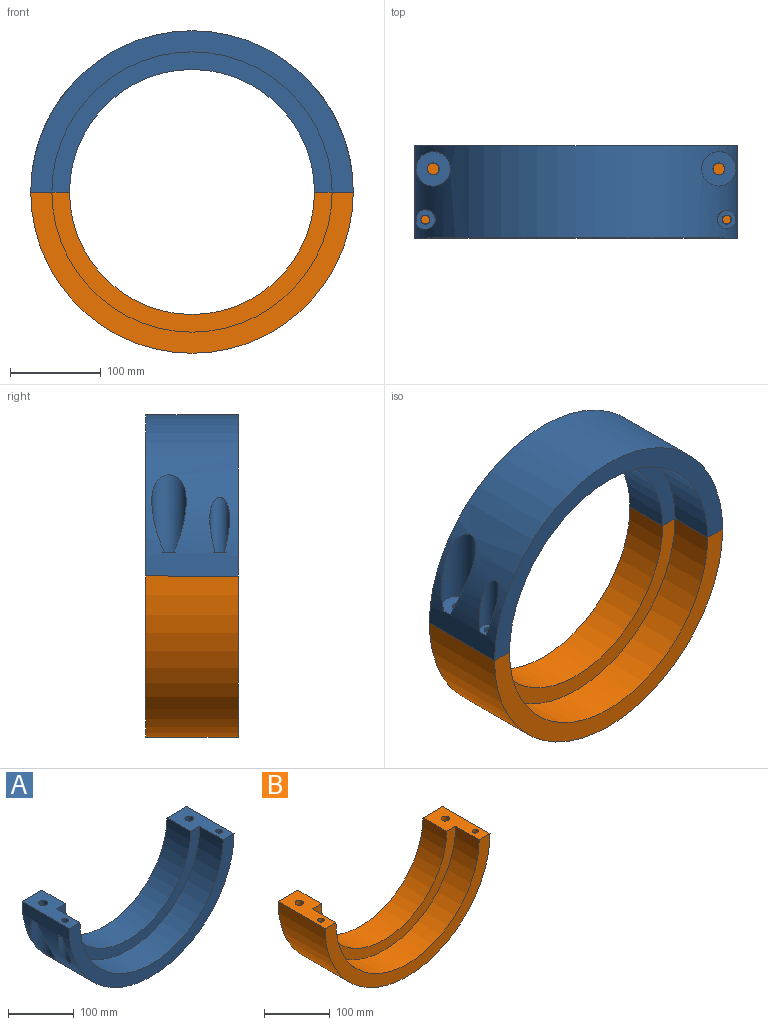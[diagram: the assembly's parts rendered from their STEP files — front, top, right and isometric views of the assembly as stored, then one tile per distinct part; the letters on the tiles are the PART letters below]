
ASSEMBLY  parts=2 mates=1
PART A: 20 faces, bbox 355.6x101.6x177.8 mm
  f0: plane 101.6x42.77mm, normal (0,0,1), area 3138.7mm2, adj f2,f3,f4,f5,f6,f7,f8,f14
  f1: plane 101.6x42.77mm, normal (0,0,1), area 3138.7mm2, adj f2,f3,f4,f5,f6,f7,f9,f15
  f2: cylinder r=177.8mm len=355.6mm, axis (0,1,0), area 49107.8mm2, adj f0,f1,f3,f4,f10,f11,f12,f13
  f3: plane 355.6x177.8mm, normal (0,-1,0), area 12164.2mm2, adj f0,f1,f2,f5
  f4: plane 355.6x177.8mm, normal (0,1,0), area 21018.4mm2, adj f0,f1,f2,f7
  f5: cylinder r=154.5mm len=308.99mm, axis (0,-1,0), area 24656.4mm2, adj f0,f1,f3,f6
  f6: plane 308.99x154.5mm, normal (0,-1,0), area 8854.2mm2, adj f0,f1,f5,f7
  f7: cylinder r=135.03mm len=270.05mm, axis (0,-1,0), area 21549.3mm2, adj f0,f1,f4,f6
  f8: cylinder r=6.6mm len=25.4mm, axis (0,0,1), area 1054mm2, adj f0,f11
  f9: cylinder r=6.6mm len=25.4mm, axis (0,0,1), area 1054mm2, adj f1,f13
  f10: cylinder r=19.05mm len=86.18mm, axis (0,0,1), area 6036.2mm2, adj f2,f11
  f11: plane 38.1x37.55mm, normal (0,0,-1), area 999.7mm2, adj f2,f8,f10
  f12: cylinder r=19.05mm len=86.18mm, axis (0,0,1), area 6036.2mm2, adj f2,f13
  f13: plane 38.1x37.55mm, normal (0,0,-1), area 999.7mm2, adj f2,f9,f12
  f14: cylinder r=5.08mm len=25.4mm, axis (0,0,1), area 810.7mm2, adj f0,f17
  f15: cylinder r=5.08mm len=25.4mm, axis (0,0,1), area 810.7mm2, adj f1,f19
  f16: cylinder r=10.97mm len=61.4mm, axis (0,0,1), area 2318.4mm2, adj f2,f17
  f17: plane 21.94x20.8mm, normal (0,0,-1), area 289.4mm2, adj f2,f14,f16
  f18: cylinder r=10.16mm len=59.93mm, axis (0,0,1), area 2165.5mm2, adj f2,f19
  f19: plane 20.32x19.99mm, normal (0,0,-1), area 242.1mm2, adj f2,f15,f18
PART B: 16 faces, bbox 355.6x101.6x177.8 mm
  f0: plane 101.6x42.77mm, normal (0,0,1), area 3158.8mm2, adj f2,f3,f4,f5,f6,f7,f10,f12
  f1: plane 101.6x42.77mm, normal (0,0,1), area 3158.8mm2, adj f2,f3,f4,f5,f6,f7,f8,f14
  f2: cylinder r=177.8mm len=355.6mm, axis (0,1,0), area 56751.2mm2, adj f0,f1,f3,f4
  f3: plane 355.6x177.8mm, normal (0,-1,0), area 12164.2mm2, adj f0,f1,f2,f5
  f4: plane 355.6x177.8mm, normal (0,1,0), area 21018.4mm2, adj f0,f1,f2,f7
  f5: cylinder r=154.5mm len=308.99mm, axis (0,-1,0), area 24656.4mm2, adj f0,f1,f3,f6
  f6: plane 308.99x154.5mm, normal (0,-1,0), area 8854.2mm2, adj f0,f1,f5,f7
  f7: cylinder r=135.03mm len=270.05mm, axis (0,-1,0), area 21549.3mm2, adj f0,f1,f4,f6
  f8: cylinder r=6.35mm len=25.4mm, axis (0,0,1), area 1013.4mm2, adj f1,f9
  f9: plane 12.7x12.7mm, normal (0,0,1), area 126.7mm2, adj f8
  f10: cylinder r=6.35mm len=25.4mm, axis (0,0,1), area 1013.4mm2, adj f0,f11
  f11: plane 12.7x12.7mm, normal (0,0,1), area 126.7mm2, adj f10
  f12: cylinder r=4.76mm len=25.4mm, axis (0,0,1), area 760.1mm2, adj f0,f13
  f13: plane 9.53x9.53mm, normal (0,0,1), area 71.3mm2, adj f12
  f14: cylinder r=4.76mm len=25.4mm, axis (0,0,1), area 760.1mm2, adj f1,f15
  f15: plane 9.53x9.53mm, normal (0,0,1), area 71.3mm2, adj f14
PLACE A rot(axis=(0,1,0),180deg) t=(-286.63,37.08,54.46)mm
PLACE B t=(-286.64,37.14,54.46)mm
MATE planar B.f0 <-> A.f1  axis (0,0,1) through (-126.84,-6.04,54.46)mm
